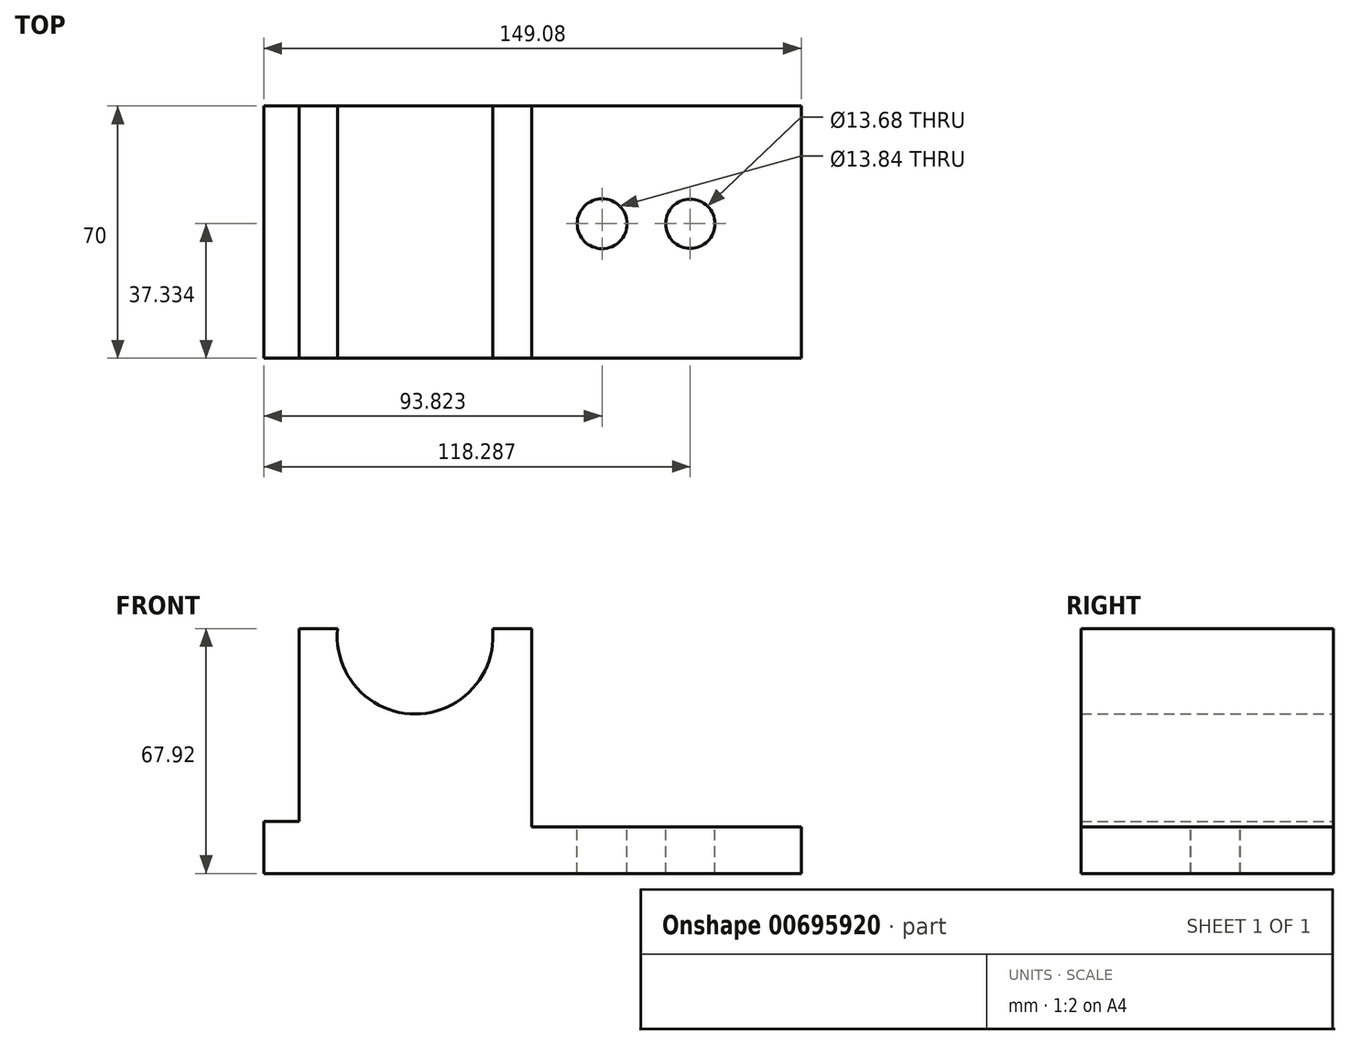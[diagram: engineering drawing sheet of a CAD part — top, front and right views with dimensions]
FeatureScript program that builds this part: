
annotation { "Feature Type Name" : "Feature", "Feature Type Description" : "" }
export const myFeature = defineFeature(function(context is Context, id is Id, definition is map)
    precondition{}
    {
        {
            var Q0;
            Q0=qCreatedBy(makeId("Front.planeOp"),FACE);
            var sketch = newSketch(context, id + "F0", { "sketchPlane" : qUnion([Q0])});
            skLineSegment(sketch, "E0", {"start": v(-43.03, 38.42) * mm, "end": v(-53.68, 38.42) * mm});
            skLineSegment(sketch, "E1", {"start": v(-53.68, 38.42) * mm, "end": v(-53.68, -15.1) * mm});
            skLineSegment(sketch, "E2", {"start": v(-53.68, -15.1) * mm, "end": v(-63.46, -15.1) * mm});
            skLineSegment(sketch, "E3", {"start": v(-63.46, -15.1) * mm, "end": v(-63.46, -29.5) * mm});
            skLineSegment(sketch, "E4", {"start": v(-63.46, -29.5) * mm, "end": v(85.62, -29.5) * mm});
            skLineSegment(sketch, "E5", {"start": v(85.62, -29.5) * mm, "end": v(85.62, -16.55) * mm});
            skLineSegment(sketch, "E6", {"start": v(85.62, -16.55) * mm, "end": v(10.8, -16.55) * mm});
            skLineSegment(sketch, "E7", {"start": v(10.8, -16.55) * mm, "end": v(10.8, 38.42) * mm});
            skLineSegment(sketch, "E8", {"start": v(10.8, 38.42) * mm, "end": v(0, 38.42) * mm});
            skArc(sketch, "E9", {"start": v(-43.03, 38.42) * mm, "mid": v(-21.51, 14.76) * mm, "end": v(0, 38.42) * mm});
            skSolve(sketch);
        }
        {
            var Q0;
            Q0 = qSketchRegion(id + "F0", true);
            extrude(context, id + "F1", {"entities" : qUnion([Q0]), "depth" : 70 * mm, "offsetDistance" : 25 * mm});
        }
        {
            var Q0;
            Q0=makeQuery(id+"F1.opExtrude","SWEPT_FACE",FACE,{"disambiguationData":[OSD([sQuery(id+"F0.wireOp",EDGE,"E6")])]});
            var sketch = newSketch(context, id + "F2", { "sketchPlane" : qUnion([Q0])});
            skCircle(sketch, "E10", {"center": v(30.36, -32.67) * mm, "radius": 6.92 * mm});
            skCircle(sketch, "E11", {"center": v(54.83, -32.67) * mm, "radius": 6.84 * mm});
            skSolve(sketch);
        }
        {
            var Q0;
            Q0 = qSketchRegion(id + "F2", true);
            extrude(context, id + "F3", {"entities" : qUnion([Q0]), "operationType" : NewBodyOperationType.REMOVE, "oppositeDirection" : true, "depth" : 25 * mm, "offsetDistance" : 25 * mm});
        }
    });
